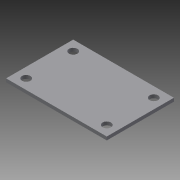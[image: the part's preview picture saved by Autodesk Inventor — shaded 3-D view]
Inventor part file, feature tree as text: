
AUTODESK INVENTOR PART (.ipt)
format: ipt  version: 2014 (Build 180170000, 170)  size: 80,384 bytes
history: native  units: in
note: dims shown in document units (in); Inventor stores cm internally (conversion verified against a paired STEP export)
features: extrude x1, sketch x1
ambient origin geometry x8: Origin, YZ Plane, XZ Plane, XY Plane, X Axis, Y Axis, Z Axis, Center Point
bodies: Solid1 (feature_tree)
feature tree (2):
  extrude  "Extrusion1"  Depth=2.5in
  sketch  "Sketch1"  dims[d0=3.75in d1=2.5in d2=1.5in d3=0.875in d4=0.3125in d5=0.125in d6=0.0in]
